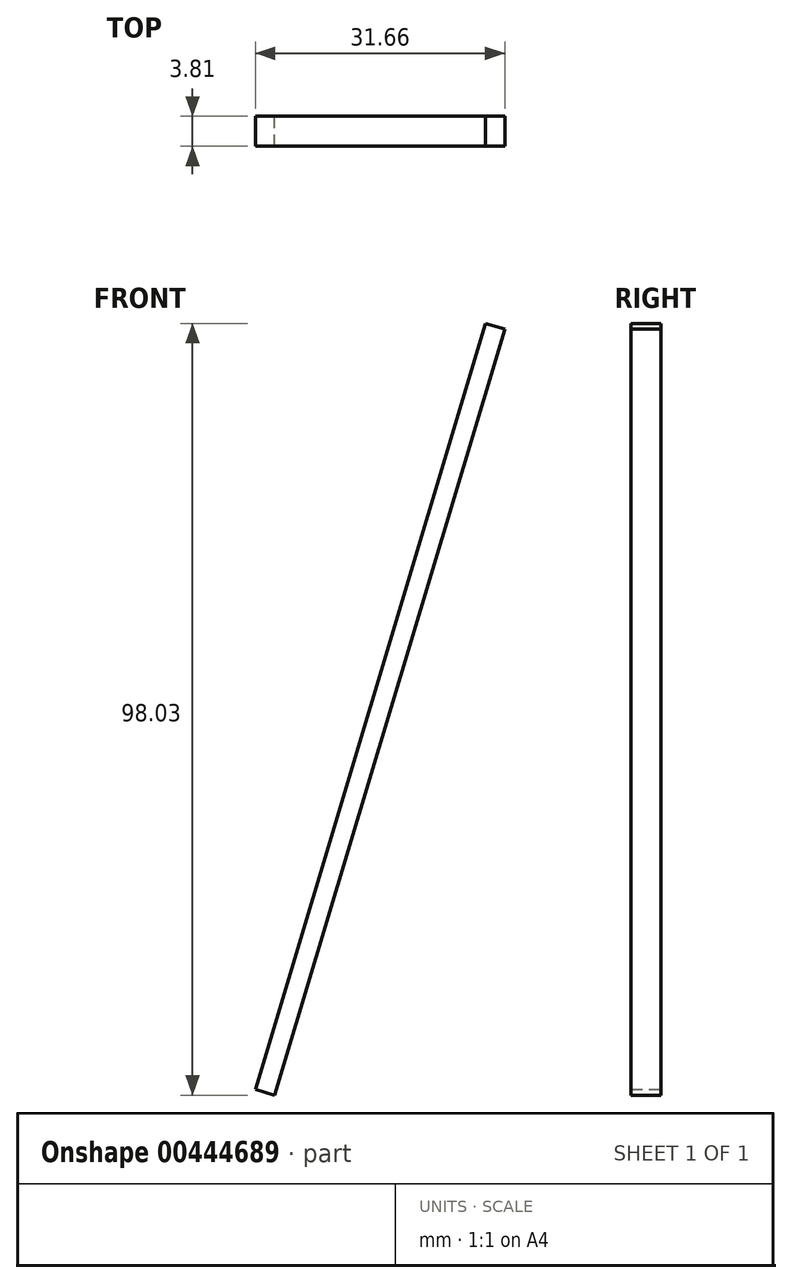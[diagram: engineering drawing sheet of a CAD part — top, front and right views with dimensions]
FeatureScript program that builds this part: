
annotation { "Feature Type Name" : "Feature", "Feature Type Description" : "" }
export const myFeature = defineFeature(function(context is Context, id is Id, definition is map)
    precondition{}
    {
        {
            var Q0;
            Q0=qCreatedBy(makeId("Front.planeOp"),FACE);
            var sketch = newSketch(context, id + "F0", { "sketchPlane" : qUnion([Q0])});
            skLineSegment(sketch, "E0", {"start": v(-102.11, 0) * mm, "end": v(-72.89, 97.3) * mm});
            skLineSegment(sketch, "E1", {"start": v(-72.89, 97.3) * mm, "end": v(-70.45, 96.57) * mm});
            skLineSegment(sketch, "E2", {"start": v(-70.45, 96.57) * mm, "end": v(-99.68, -0.73) * mm});
            skLineSegment(sketch, "E3", {"start": v(-99.68, -0.73) * mm, "end": v(-102.11, 0) * mm});
            skSolve(sketch);
        }
        {
            var Q0;
            Q0 = qSketchRegion(id + "F0", true);
            extrude(context, id + "F1", {"entities" : qUnion([Q0]), "depth" : 3.8 * mm});
        }
    });
